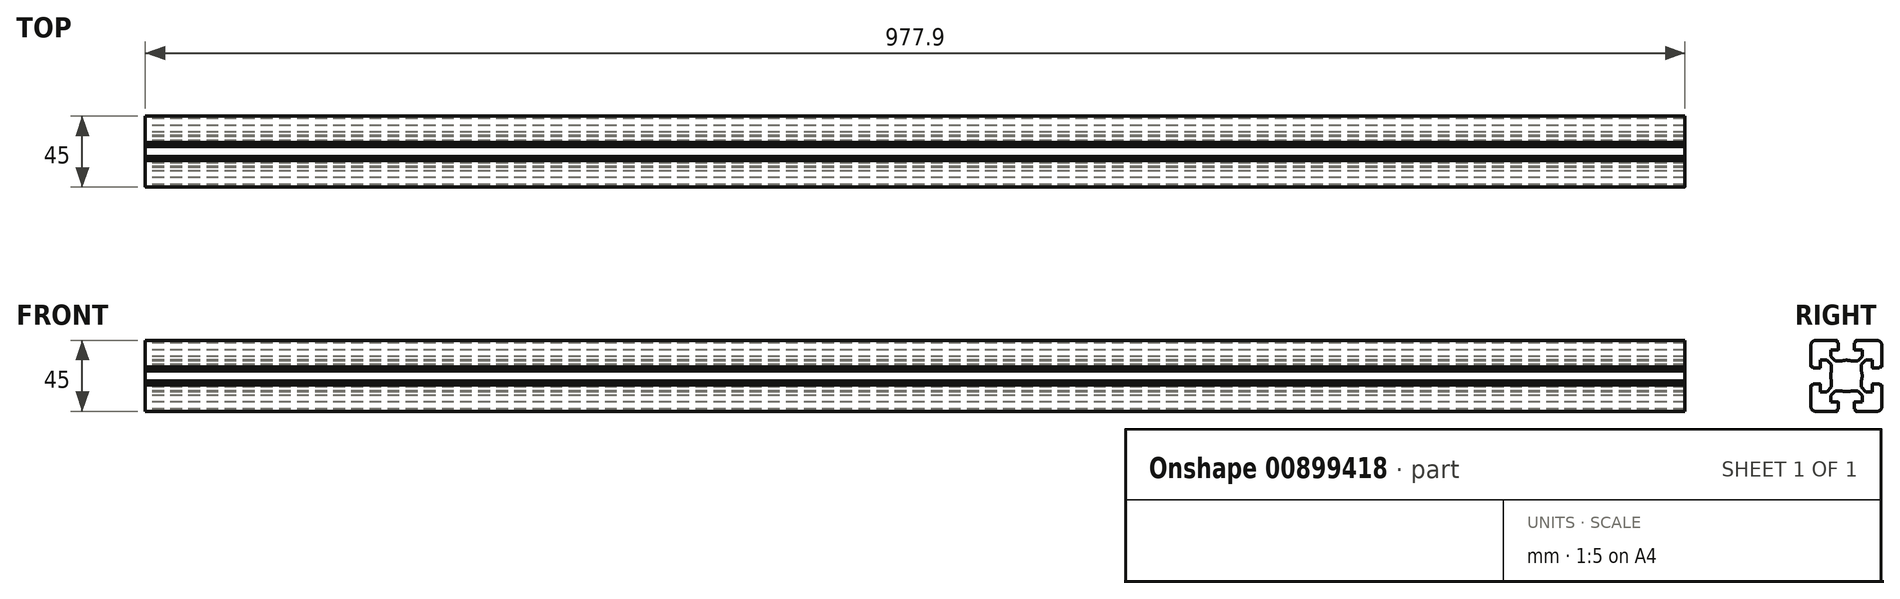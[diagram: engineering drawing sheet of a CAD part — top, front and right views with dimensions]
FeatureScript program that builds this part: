
annotation { "Feature Type Name" : "Feature", "Feature Type Description" : "" }
export const myFeature = defineFeature(function(context is Context, id is Id, definition is map)
    precondition{}
    {
        {
            var Q0;
            Q0=qCreatedBy(makeId("Right.planeOp"),FACE);
            var sketch = newSketch(context, id + "F0", { "sketchPlane" : qUnion([Q0])});
            skLineSegment(sketch, "E0", {"start": v(-20.09, -10.29) * mm, "end": v(-21.29, -10.29) * mm});
            skArc(sketch, "E1", {"start": v(-21.29, -10.29) * mm, "mid": v(-21.5, -10.38) * mm, "end": v(-21.59, -10.59) * mm});
            skLineSegment(sketch, "E2", {"start": v(-21.59, -10.59) * mm, "end": v(-21.59, -23.99) * mm});
            skArc(sketch, "E3", {"start": v(-21.59, -23.99) * mm, "mid": v(-20.7, -26.11) * mm, "end": v(-18.59, -26.99) * mm});
            skLineSegment(sketch, "E4", {"start": v(-18.59, -26.99) * mm, "end": v(-5.19, -26.99) * mm});
            skArc(sketch, "E5", {"start": v(-5.19, -26.99) * mm, "mid": v(-4.98, -26.9) * mm, "end": v(-4.89, -26.69) * mm});
            skLineSegment(sketch, "E6", {"start": v(-4.89, -26.69) * mm, "end": v(-4.89, -25.49) * mm});
            skLineSegment(sketch, "E7", {"start": v(-4.89, -25.49) * mm, "end": v(-4.39, -25.49) * mm});
            skArc(sketch, "E8", {"start": v(-4.39, -25.49) * mm, "mid": v(-4.18, -25.4) * mm, "end": v(-4.09, -25.19) * mm});
            skLineSegment(sketch, "E9", {"start": v(-4.09, -25.19) * mm, "end": v(-4.09, -21.29) * mm});
            skArc(sketch, "E10", {"start": v(-4.09, -21.29) * mm, "mid": v(-4.18, -21.08) * mm, "end": v(-4.39, -20.99) * mm});
            skLineSegment(sketch, "E11", {"start": v(-4.39, -20.99) * mm, "end": v(-9.14, -20.99) * mm});
            skLineSegment(sketch, "E12", {"start": v(-9.14, -20.99) * mm, "end": v(-9.14, -16.88) * mm});
            skLineSegment(sketch, "E13", {"start": v(-9.14, -16.88) * mm, "end": v(-6.25, -13.99) * mm});
            skLineSegment(sketch, "E14", {"start": v(-6.25, -13.99) * mm, "end": v(-2.21, -13.99) * mm});
            skArc(sketch, "E15", {"start": v(-2.21, -13.99) * mm, "mid": v(0.91, -14.49) * mm, "end": v(4.03, -13.99) * mm});
            skLineSegment(sketch, "E16", {"start": v(-20.09, -10.29) * mm, "end": v(-20.09, -9.79) * mm});
            skArc(sketch, "E17", {"start": v(-20.09, -9.79) * mm, "mid": v(-20, -9.58) * mm, "end": v(-19.79, -9.49) * mm});
            skLineSegment(sketch, "E18", {"start": v(-19.79, -9.49) * mm, "end": v(-15.89, -9.49) * mm});
            skArc(sketch, "E19", {"start": v(-15.89, -9.49) * mm, "mid": v(-15.68, -9.58) * mm, "end": v(-15.59, -9.79) * mm});
            skLineSegment(sketch, "E20", {"start": v(-15.59, -9.79) * mm, "end": v(-15.59, -14.54) * mm});
            skLineSegment(sketch, "E21", {"start": v(-15.59, -14.54) * mm, "end": v(-11.48, -14.54) * mm});
            skLineSegment(sketch, "E22", {"start": v(-11.48, -14.54) * mm, "end": v(-8.59, -11.65) * mm});
            skLineSegment(sketch, "E23", {"start": v(-8.59, -11.65) * mm, "end": v(-8.59, -7.61) * mm});
            skLineSegment(sketch, "E24", {"start": v(29.82, -4.49) * mm, "end": v(-31.05, -4.49) * mm});
            skLineSegment(sketch, "E25.MirrorCS", {"start": v(6.71, -25.49) * mm, "end": v(6.21, -25.49) * mm});
            skArc(sketch, "E26.MirrorCS", {"start": v(7.01, -26.99) * mm, "mid": v(6.8, -26.9) * mm, "end": v(6.71, -26.69) * mm});
            skLineSegment(sketch, "E27.MirrorCS", {"start": v(10.41, -11.65) * mm, "end": v(10.41, -7.61) * mm});
            skArc(sketch, "E28.MirrorCS", {"start": v(6.21, -25.49) * mm, "mid": v(6, -25.4) * mm, "end": v(5.91, -25.19) * mm});
            skLineSegment(sketch, "E29.MirrorCS", {"start": v(6.71, -26.69) * mm, "end": v(6.71, -25.49) * mm});
            skArc(sketch, "E30.MirrorCS", {"start": v(5.91, -21.29) * mm, "mid": v(6, -21.08) * mm, "end": v(6.21, -20.99) * mm});
            skLineSegment(sketch, "E31.MirrorCS", {"start": v(10.96, -16.88) * mm, "end": v(8.07, -13.99) * mm});
            skLineSegment(sketch, "E32.MirrorCS", {"start": v(13.3, -14.54) * mm, "end": v(10.41, -11.65) * mm});
            skLineSegment(sketch, "E33.MirrorCS", {"start": v(17.41, -14.54) * mm, "end": v(13.3, -14.54) * mm});
            skLineSegment(sketch, "E34.MirrorCS", {"start": v(17.41, -9.79) * mm, "end": v(17.41, -14.54) * mm});
            skLineSegment(sketch, "E35.MirrorCS", {"start": v(6.21, -20.99) * mm, "end": v(10.96, -20.99) * mm});
            skLineSegment(sketch, "E36.MirrorCS", {"start": v(8.07, -13.99) * mm, "end": v(4.03, -13.99) * mm});
            skArc(sketch, "E37.MirrorCS", {"start": v(4.03, -13.99) * mm, "mid": v(0.91, -14.49) * mm, "end": v(-2.21, -13.99) * mm});
            skLineSegment(sketch, "E38.MirrorCS", {"start": v(10.96, -20.99) * mm, "end": v(10.96, -16.88) * mm});
            skLineSegment(sketch, "E39.MirrorCS", {"start": v(5.91, -25.19) * mm, "end": v(5.91, -21.29) * mm});
            skArc(sketch, "E40.MirrorCS", {"start": v(23.41, -23.99) * mm, "mid": v(22.53, -26.11) * mm, "end": v(20.41, -26.99) * mm});
            skLineSegment(sketch, "E41.MirrorCS", {"start": v(20.41, -26.99) * mm, "end": v(7.01, -26.99) * mm});
            skLineSegment(sketch, "E42.MirrorCS", {"start": v(23.41, -10.59) * mm, "end": v(23.41, -23.99) * mm});
            skArc(sketch, "E43.MirrorCS", {"start": v(17.71, -9.49) * mm, "mid": v(17.5, -9.58) * mm, "end": v(17.41, -9.79) * mm});
            skArc(sketch, "E44.MirrorCS", {"start": v(23.11, -10.29) * mm, "mid": v(23.32, -10.38) * mm, "end": v(23.41, -10.59) * mm});
            skLineSegment(sketch, "E45.MirrorCS", {"start": v(21.91, -10.29) * mm, "end": v(21.91, -9.79) * mm});
            skLineSegment(sketch, "E46.MirrorCS", {"start": v(21.91, -10.29) * mm, "end": v(23.11, -10.29) * mm});
            skArc(sketch, "E47.MirrorCS", {"start": v(21.91, -9.79) * mm, "mid": v(21.82, -9.58) * mm, "end": v(21.61, -9.49) * mm});
            skLineSegment(sketch, "E48.MirrorCS", {"start": v(21.61, -9.49) * mm, "end": v(17.71, -9.49) * mm});
            skLineSegment(sketch, "E49.MirrorCS", {"start": v(6.71, 16.51) * mm, "end": v(6.21, 16.51) * mm});
            skArc(sketch, "E50.MirrorCS", {"start": v(-4.39, 16.51) * mm, "mid": v(-4.18, 16.42) * mm, "end": v(-4.09, 16.21) * mm});
            skLineSegment(sketch, "E51.MirrorCS", {"start": v(-4.89, 16.51) * mm, "end": v(-4.39, 16.51) * mm});
            skArc(sketch, "E52.MirrorCS", {"start": v(5.91, 12.31) * mm, "mid": v(6, 12.1) * mm, "end": v(6.21, 12.01) * mm});
            skLineSegment(sketch, "E53.MirrorCS", {"start": v(6.71, 17.71) * mm, "end": v(6.71, 16.51) * mm});
            skLineSegment(sketch, "E54.MirrorCS", {"start": v(-4.89, 17.71) * mm, "end": v(-4.89, 16.51) * mm});
            skArc(sketch, "E55.MirrorCS", {"start": v(-5.19, 18.01) * mm, "mid": v(-4.98, 17.92) * mm, "end": v(-4.89, 17.71) * mm});
            skArc(sketch, "E56.MirrorCS", {"start": v(-4.09, 12.31) * mm, "mid": v(-4.18, 12.1) * mm, "end": v(-4.39, 12.01) * mm});
            skArc(sketch, "E57.MirrorCS", {"start": v(7.01, 18.01) * mm, "mid": v(6.8, 17.92) * mm, "end": v(6.71, 17.71) * mm});
            skArc(sketch, "E58.MirrorCS", {"start": v(6.21, 16.51) * mm, "mid": v(6, 16.42) * mm, "end": v(5.91, 16.21) * mm});
            skArc(sketch, "E59.MirrorCS", {"start": v(23.11, 1.31) * mm, "mid": v(23.32, 1.4) * mm, "end": v(23.41, 1.61) * mm});
            skLineSegment(sketch, "E60.MirrorCS", {"start": v(21.91, 1.31) * mm, "end": v(21.91, 0.81) * mm});
            skArc(sketch, "E61.MirrorCS", {"start": v(-15.89, 0.51) * mm, "mid": v(-15.68, 0.6) * mm, "end": v(-15.59, 0.81) * mm});
            skArc(sketch, "E62.MirrorCS", {"start": v(-21.29, 1.31) * mm, "mid": v(-21.5, 1.4) * mm, "end": v(-21.59, 1.61) * mm});
            skArc(sketch, "E63.MirrorCS", {"start": v(17.71, 0.51) * mm, "mid": v(17.5, 0.6) * mm, "end": v(17.41, 0.81) * mm});
            skArc(sketch, "E64.MirrorCS", {"start": v(21.91, 0.81) * mm, "mid": v(21.82, 0.6) * mm, "end": v(21.61, 0.51) * mm});
            skLineSegment(sketch, "E65.MirrorCS", {"start": v(21.91, 1.31) * mm, "end": v(23.11, 1.31) * mm});
            skArc(sketch, "E66.MirrorCS", {"start": v(14.31, 5.31) * mm, "mid": v(14.1, 5.4) * mm, "end": v(14.01, 5.61) * mm});
            skArc(sketch, "E67.MirrorCS", {"start": v(-20.09, 0.81) * mm, "mid": v(-20, 0.6) * mm, "end": v(-19.79, 0.51) * mm});
            skLineSegment(sketch, "E68.MirrorCS", {"start": v(-20.09, 1.31) * mm, "end": v(-21.29, 1.31) * mm});
            skLineSegment(sketch, "E69.MirrorCS", {"start": v(-20.09, 1.31) * mm, "end": v(-20.09, 0.81) * mm});
            skLineSegment(sketch, "E70.MirrorCS", {"start": v(8.07, 5.01) * mm, "end": v(4.03, 5.01) * mm});
            skLineSegment(sketch, "E71.MirrorCS", {"start": v(-4.09, 16.21) * mm, "end": v(-4.09, 12.31) * mm});
            skLineSegment(sketch, "E72.MirrorCS", {"start": v(-9.14, 12.01) * mm, "end": v(-9.14, 7.9) * mm});
            skLineSegment(sketch, "E73.MirrorCS", {"start": v(-15.59, 5.56) * mm, "end": v(-11.48, 5.56) * mm});
            skLineSegment(sketch, "E74.MirrorCS", {"start": v(-4.39, 12.01) * mm, "end": v(-9.14, 12.01) * mm});
            skLineSegment(sketch, "E75.MirrorCS", {"start": v(-9.14, 7.9) * mm, "end": v(-6.25, 5.01) * mm});
            skLineSegment(sketch, "E76.MirrorCS", {"start": v(10.96, 12.01) * mm, "end": v(10.96, 7.9) * mm});
            skArc(sketch, "E77.MirrorCS", {"start": v(-21.59, 15.01) * mm, "mid": v(-20.7, 17.13) * mm, "end": v(-18.59, 18.01) * mm});
            skLineSegment(sketch, "E78.MirrorCS", {"start": v(23.41, 1.61) * mm, "end": v(23.41, 15.01) * mm});
            skLineSegment(sketch, "E79.MirrorCS", {"start": v(13.3, 5.56) * mm, "end": v(10.41, 2.67) * mm});
            skLineSegment(sketch, "E80.MirrorCS", {"start": v(-8.59, 2.67) * mm, "end": v(-8.59, -1.37) * mm});
            skLineSegment(sketch, "E81.MirrorCS", {"start": v(-15.59, 0.81) * mm, "end": v(-15.59, 5.56) * mm});
            skLineSegment(sketch, "E82.MirrorCS", {"start": v(10.41, 2.67) * mm, "end": v(10.41, -1.37) * mm});
            skLineSegment(sketch, "E83.MirrorCS", {"start": v(-18.59, 18.01) * mm, "end": v(-5.19, 18.01) * mm});
            skLineSegment(sketch, "E84.MirrorCS", {"start": v(10.96, 7.9) * mm, "end": v(8.07, 5.01) * mm});
            skLineSegment(sketch, "E85.MirrorCS", {"start": v(17.41, 5.56) * mm, "end": v(13.3, 5.56) * mm});
            skArc(sketch, "E86.MirrorCS", {"start": v(23.41, 15.01) * mm, "mid": v(22.53, 17.13) * mm, "end": v(20.41, 18.01) * mm});
            skLineSegment(sketch, "E87.MirrorCS", {"start": v(5.91, 16.21) * mm, "end": v(5.91, 12.31) * mm});
            skLineSegment(sketch, "E88.MirrorCS", {"start": v(17.41, 0.81) * mm, "end": v(17.41, 5.56) * mm});
            skLineSegment(sketch, "E89.MirrorCS", {"start": v(-11.48, 5.56) * mm, "end": v(-8.59, 2.67) * mm});
            skLineSegment(sketch, "E90.MirrorCS", {"start": v(-6.25, 5.01) * mm, "end": v(-2.21, 5.01) * mm});
            skLineSegment(sketch, "E91.MirrorCS", {"start": v(-21.59, 1.61) * mm, "end": v(-21.59, 15.01) * mm});
            skArc(sketch, "E92.MirrorCS", {"start": v(4.03, 5.01) * mm, "mid": v(0.91, 5.51) * mm, "end": v(-2.21, 5.01) * mm});
            skLineSegment(sketch, "E93.MirrorCS", {"start": v(6.21, 12.01) * mm, "end": v(10.96, 12.01) * mm});
            skArc(sketch, "E94.MirrorCS", {"start": v(-2.21, 5.01) * mm, "mid": v(0.91, 5.51) * mm, "end": v(4.03, 5.01) * mm});
            skLineSegment(sketch, "E95.MirrorCS", {"start": v(20.41, 18.01) * mm, "end": v(7.01, 18.01) * mm});
            skLineSegment(sketch, "E96.MirrorCS", {"start": v(-19.79, 0.51) * mm, "end": v(-15.89, 0.51) * mm});
            skLineSegment(sketch, "E97.MirrorCS", {"start": v(21.61, 0.51) * mm, "end": v(17.71, 0.51) * mm});
            skLineSegment(sketch, "E98.MirrorCS", {"start": v(0.91, -27.65) * mm, "end": v(0.91, 19.82) * mm});
            skArc(sketch, "E99", {"start": v(-8.59, -1.37) * mm, "mid": v(-9.09, -4.49) * mm, "end": v(-8.59, -7.61) * mm});
            skArc(sketch, "E100", {"start": v(10.41, -7.61) * mm, "mid": v(10.91, -4.49) * mm, "end": v(10.41, -1.37) * mm});
            skSolve(sketch);
        }
        {
            var Q0;
            Q0=qSketchRegion(id+"F0",true);
            extrude(context, id + "F1", {"entities" : qUnion([Q0]), "depth" : 977.9 * mm, "offsetDistance" : 25.4 * mm});
        }
    });
